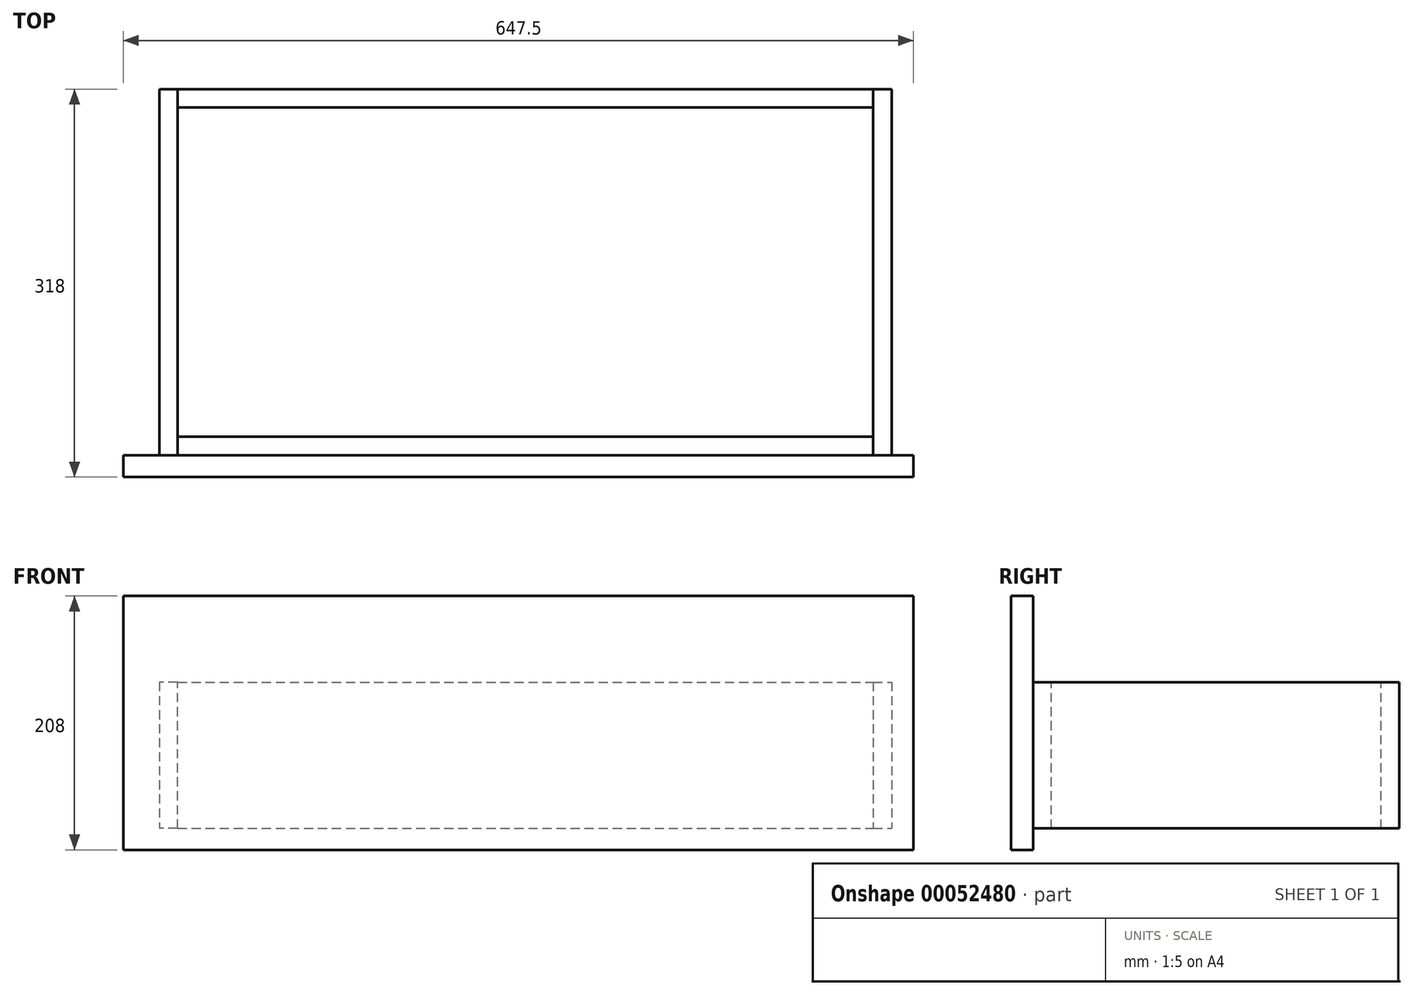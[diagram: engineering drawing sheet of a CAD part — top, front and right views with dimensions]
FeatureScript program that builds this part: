
annotation { "Feature Type Name" : "Feature", "Feature Type Description" : "" }
export const myFeature = defineFeature(function(context is Context, id is Id, definition is map)
    precondition{}
    {
        {
            var Q0;
            Q0=qCreatedBy(makeId("Front.planeOp"),FACE);
            var sketch = newSketch(context, id + "F0", { "sketchPlane" : qUnion([Q0])});
            skLineSegment(sketch, "E0.bottom", {"start": v(-285, 0) * mm, "end": v(285, 0) * mm});
            skLineSegment(sketch, "E0.top", {"start": v(-285, 120) * mm, "end": v(285, 120) * mm});
            skLineSegment(sketch, "E0.left", {"start": v(-285, 0) * mm, "end": v(-285, 120) * mm});
            skLineSegment(sketch, "E0.right", {"start": v(285, 0) * mm, "end": v(285, 120) * mm});
            skSolve(sketch);
        }
        {
            var Q0;
            Q0=makeQuery(id+"F0.imprint","IMPRINT",FACE,{"disambiguationData":[TD([[makeQuery(id+"F0.imprint","IMPRINT",EDGE,{"derivedFrom":sQuery(id+"F0.wireOp",EDGE,"E0.bottom")}),1.0]])]});
            extrude(context, id + "F1", {"entities" : qUnion([Q0]), "depth" : 15 * mm});
        }
        {
            var Q0;
            Q0=makeQuery(id+"F1.opExtrude","CAP_FACE",FACE,{"disambiguationData":[OSD([sQuery(id+"F0.wireOp",EDGE,"E0.bottom"),sQuery(id+"F0.wireOp",EDGE,"E0.top"),sQuery(id+"F0.wireOp",EDGE,"E0.left"),sQuery(id+"F0.wireOp",EDGE,"E0.right")])],"isStart":false});
            var sketch = newSketch(context, id + "F2", { "sketchPlane" : qUnion([Q0])});
            skLineSegment(sketch, "E1.bottom", {"start": v(285, 120) * mm, "end": v(300, 120) * mm});
            skLineSegment(sketch, "E1.top", {"start": v(285, 0) * mm, "end": v(300, 0) * mm});
            skLineSegment(sketch, "E1.left", {"start": v(285, 120) * mm, "end": v(285, 0) * mm});
            skLineSegment(sketch, "E1.right", {"start": v(300, 120) * mm, "end": v(300, 0) * mm});
            skLineSegment(sketch, "E2.bottom", {"start": v(-285, 120) * mm, "end": v(-300, 120) * mm});
            skLineSegment(sketch, "E2.top", {"start": v(-285, 0) * mm, "end": v(-300, 0) * mm});
            skLineSegment(sketch, "E2.left", {"start": v(-285, 120) * mm, "end": v(-285, 0) * mm});
            skLineSegment(sketch, "E2.right", {"start": v(-300, 120) * mm, "end": v(-300, 0) * mm});
            skSolve(sketch);
        }
        {
            var Q0;
            Q0=qSketchRegion(id+"F2",true);
            extrude(context, id + "F3", {"entities" : qUnion([Q0]), "oppositeDirection" : true, "depth" : 300 * mm});
        }
        {
            var Q0;
            Q0=makeQuery(id+"F3.opExtrude","SWEPT_FACE",FACE,{"disambiguationData":[OSD([sQuery(id+"F2.wireOp",EDGE,"E1.left")])]});
            var sketch = newSketch(context, id + "F4", { "sketchPlane" : qUnion([Q0])});
            skLineSegment(sketch, "E3.bottom", {"start": v(-285, 120) * mm, "end": v(-270, 120) * mm});
            skLineSegment(sketch, "E3.top", {"start": v(-285, 0) * mm, "end": v(-270, 0) * mm});
            skLineSegment(sketch, "E3.left", {"start": v(-285, 120) * mm, "end": v(-285, 0) * mm});
            skLineSegment(sketch, "E3.right", {"start": v(-270, 120) * mm, "end": v(-270, 0) * mm});
            skSolve(sketch);
        }
        {
            var Q0;
            Q0=qSketchRegion(id+"F4",true);
            extrude(context, id + "F5", {"entities" : qUnion([Q0]), "endBound" : BoundingType.UP_TO_NEXT, "depth" : 25 * mm});
        }
        {
            var Q0;
            Q0=makeQuery(id+"F1.opExtrude","CAP_FACE",FACE,{"disambiguationData":[OSD([sQuery(id+"F0.wireOp",EDGE,"E0.bottom"),sQuery(id+"F0.wireOp",EDGE,"E0.top"),sQuery(id+"F0.wireOp",EDGE,"E0.left"),sQuery(id+"F0.wireOp",EDGE,"E0.right")])],"isStart":false});
            var sketch = newSketch(context, id + "F6", { "sketchPlane" : qUnion([Q0])});
            skLineSegment(sketch, "E4.bottom", {"start": v(-329.5, 190.5) * mm, "end": v(318, 190.5) * mm});
            skLineSegment(sketch, "E4.top", {"start": v(-329.5, -17.5) * mm, "end": v(318, -17.5) * mm});
            skLineSegment(sketch, "E4.left", {"start": v(-329.5, 190.5) * mm, "end": v(-329.5, -17.5) * mm});
            skLineSegment(sketch, "E4.right", {"start": v(318, 190.5) * mm, "end": v(318, -17.5) * mm});
            skPoint(sketch, "E5.startSnap0", {"position": v(-5.75, -17.5) * mm});
            skSolve(sketch);
        }
        {
            var Q0;
            Q0=qSketchRegion(id+"F6",true);
            extrude(context, id + "F7", {"entities" : qUnion([Q0]), "depth" : 18 * mm});
        }
    });
